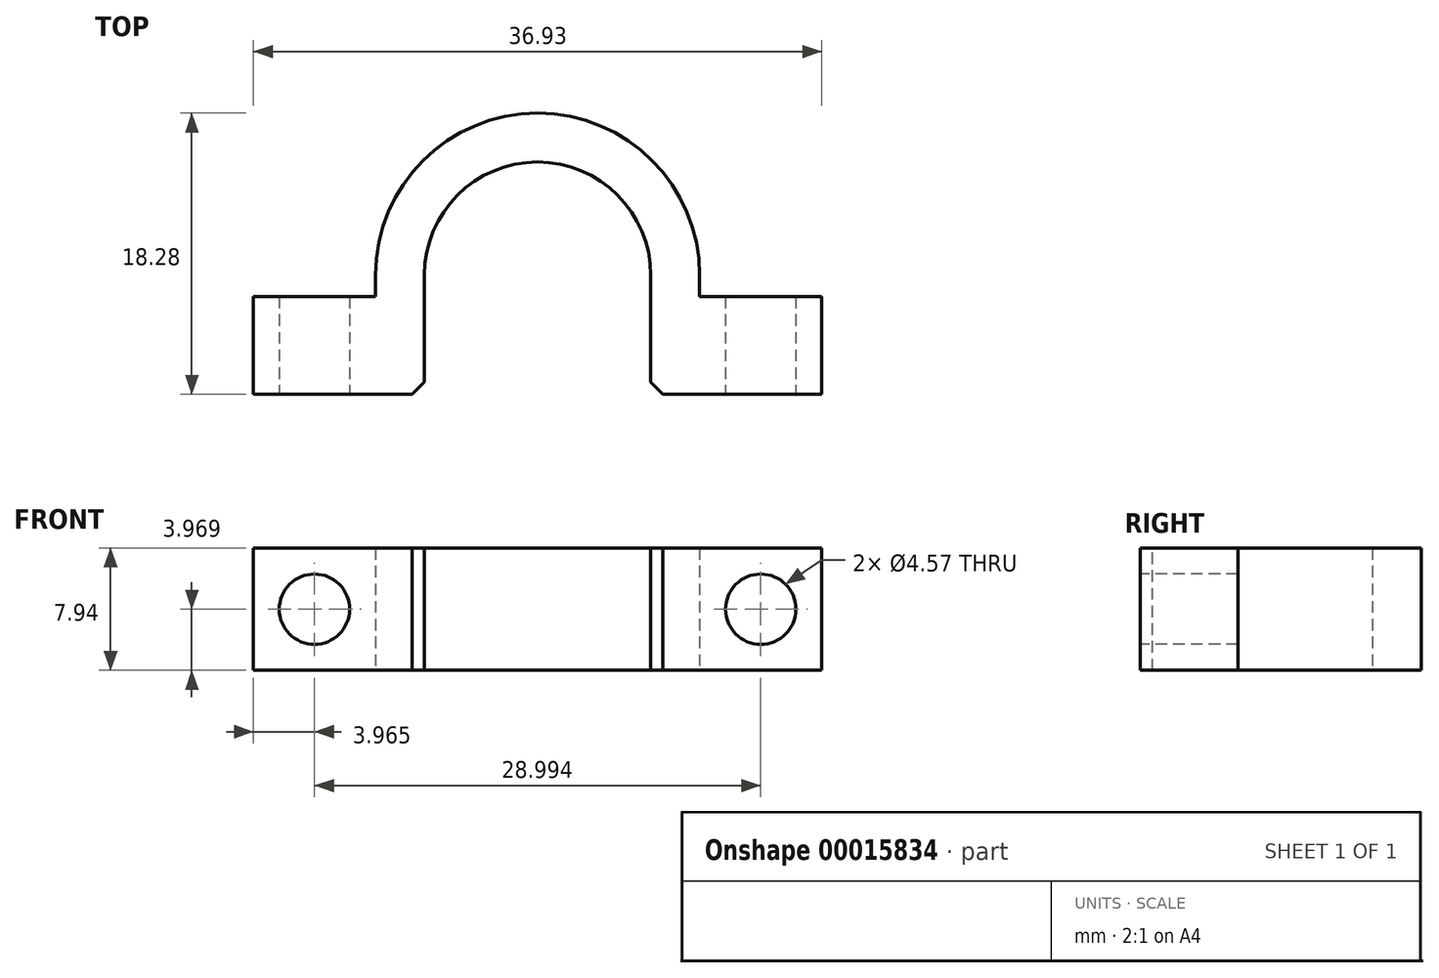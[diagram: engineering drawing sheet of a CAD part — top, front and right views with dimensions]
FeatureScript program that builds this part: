
annotation { "Feature Type Name" : "Feature", "Feature Type Description" : "" }
export const myFeature = defineFeature(function(context is Context, id is Id, definition is map)
    precondition{}
    {
        {
            var Q0;
            Q0=qCreatedBy(makeId("Top.planeOp"),FACE);
            var sketch = newSketch(context, id + "F0", { "sketchPlane" : qUnion([Q0])});
            skLineSegment(sketch, "E0", {"start": v(0, 0) * mm, "end": v(-3.18, 0) * mm, "construction": true});
            skLineSegment(sketch, "E1", {"start": v(-3.17, 0) * mm, "end": v(-17.88, 0) * mm, "construction": true});
            skLineSegment(sketch, "E2", {"start": v(-17.88, 0) * mm, "end": v(-21.06, 0) * mm, "construction": true});
            skLineSegment(sketch, "E3", {"start": v(0, 0) * mm, "end": v(0, -1.4) * mm});
            skLineSegment(sketch, "E4", {"start": v(-3.18, 0) * mm, "end": v(-3.18, -7.75) * mm});
            skLineSegment(sketch, "E5", {"start": v(0, -1.4) * mm, "end": v(7.94, -1.4) * mm});
            skLineSegment(sketch, "E6", {"start": v(7.94, -1.4) * mm, "end": v(7.94, -7.75) * mm});
            skLineSegment(sketch, "E7", {"start": v(7.94, -7.75) * mm, "end": v(-3.17, -7.75) * mm});
            skLineSegment(sketch, "E8", {"start": v(-17.88, 0) * mm, "end": v(-17.88, -7.75) * mm});
            skLineSegment(sketch, "E9", {"start": v(-17.88, -7.75) * mm, "end": v(-29, -7.75) * mm});
            skLineSegment(sketch, "E10", {"start": v(-29, -7.75) * mm, "end": v(-29, -1.4) * mm});
            skLineSegment(sketch, "E11", {"start": v(-29, -1.4) * mm, "end": v(-21.06, -1.4) * mm});
            skLineSegment(sketch, "E12", {"start": v(-21.06, -1.4) * mm, "end": v(-21.06, 0) * mm});
            skArc(sketch, "E13", {"start": v(-3.17, 0) * mm, "mid": v(-10.53, 7.35) * mm, "end": v(-17.88, 0) * mm});
            skArc(sketch, "E14", {"start": v(0, 0) * mm, "mid": v(-10.53, 10.53) * mm, "end": v(-21.06, 0) * mm});
            skLineSegment(sketch, "E15", {"start": v(-10.53, 0) * mm, "end": v(-10.53, 7.35) * mm});
            skSolve(sketch);
        }
        {
            var Q0;
            Q0 = qSketchRegion(id + "F0", true);
            extrude(context, id + "F1", {"entities" : qUnion([Q0]), "depth" : 7.94 * mm});
        }
        {
            var Q0;
            Q0=makeQuery(id+"F1.opExtrude","SWEPT_FACE",FACE,{"disambiguationData":[OSD([sQuery(id+"F0.wireOp",EDGE,"E9")])]});
            var sketch = newSketch(context, id + "F2", { "sketchPlane" : qUnion([Q0])});
            skLineSegment(sketch, "E16", {"start": v(-29, 3.97) * mm, "end": v(-25.03, 3.97) * mm});
            skLineSegment(sketch, "E17", {"start": v(7.94, 3.97) * mm, "end": v(3.97, 3.97) * mm});
            skCircle(sketch, "E18", {"center": v(-25.03, 3.97) * mm, "radius": 2.29 * mm});
            skCircle(sketch, "E19", {"center": v(3.97, 3.97) * mm, "radius": 2.29 * mm});
            skSolve(sketch);
        }
        {
            var Q0;
            Q0 = qSketchRegion(id + "F2", true);
            var Q1;
            Q1=makeQuery(id+"F1.opExtrude","SWEPT_FACE",FACE,{"disambiguationData":[OSD([sQuery(id+"F0.wireOp",EDGE,"E11")])]});
            extrude(context, id + "F3", {"entities" : qUnion([Q0]), "operationType" : NewBodyOperationType.REMOVE, "endBound" : BoundingType.UP_TO_SURFACE, "oppositeDirection" : true, "endBoundEntityFace" : qUnion([Q1]), "depth" : 25.4 * mm});
        }
        {
            var Q0;
            Q0=makeQuery(id+"F1.opExtrude","SWEPT_EDGE",EDGE,{"disambiguationData":[OSD([sQuery(id+"F0.wireOp",EDGE,"E8"),sQuery(id+"F0.wireOp",EDGE,"E9")])]});
            var Q1;
            Q1=makeQuery(id+"F1.opExtrude","SWEPT_EDGE",EDGE,{"disambiguationData":[OSD([sQuery(id+"F0.wireOp",EDGE,"E4"),sQuery(id+"F0.wireOp",EDGE,"E7")])]});
            chamfer(context, id + "F4", {"entities" : qUnion([Q0, Q1]), "width" : 0.8 * mm, "tangentPropagation" : true});
        }
    });
